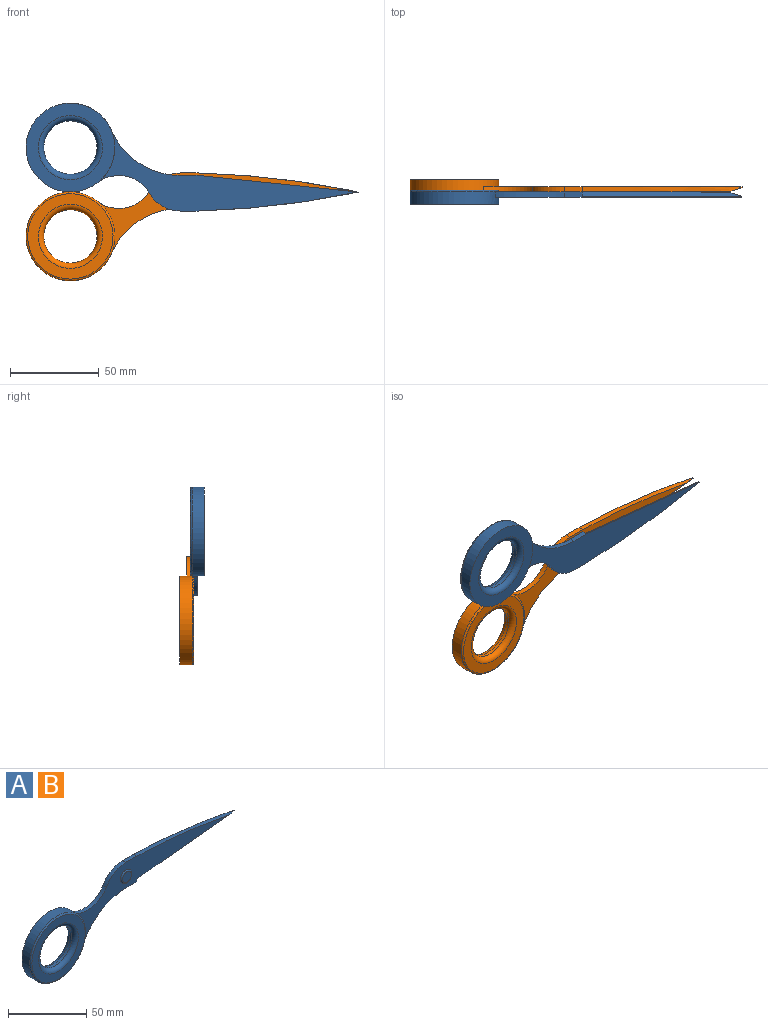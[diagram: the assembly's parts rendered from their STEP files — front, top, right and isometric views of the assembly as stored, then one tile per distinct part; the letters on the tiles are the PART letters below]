
ASSEMBLY  parts=2 mates=1
PART A: 20 faces, bbox 188.9x8x62.8 mm
  f0: plane 138.19x45.59mm, normal (0,-1,0), area 1559.5mm2, adj f1,f3,f4,f6,f7,f9,f14,f15
  f1: cylinder r=20mm len=27.95mm, axis (0,1,0), area 95.5mm2, adj f0,f2,f4,f5
  f2: plane 145.66x45.59mm, normal (0,1,0), area 1836.2mm2, adj f1,f3,f4,f5,f6,f7,f8,f9
  f3: plane 10x3mm, normal (0,0,1), area 30mm2, adj f0,f2,f4,f9
  f4: cylinder r=20mm len=17.71mm, axis (0,1,0), area 65.2mm2, adj f0,f1,f2,f3
  f5: cylinder r=25mm len=50mm, axis (0,1,0), area 1004mm2, adj f1,f2,f6,f11,f17
  f6: cylinder r=42.31mm len=38.86mm, axis (0,1,0), area 147.8mm2, adj f0,f2,f5,f7
  f7: plane 10x3mm, normal (0,0,-1), area 30mm2, adj f0,f2,f6,f8,f14
  f8: plane 90x9.3mm, normal (0.1,0,-0.99), area 63.7mm2, adj f2,f7,f9,f15
  f9: cylinder r=500mm len=90mm, axis (0,1,0), area 263.6mm2, adj f0,f2,f3,f8,f15
  f10: plane 48x48mm, normal (0,-1,0), area 791.7mm2, adj f16,f17
  f11: plane 50x50mm, normal (0,1,0), area 945.6mm2, adj f5,f18
  f12: cylinder r=15mm len=30mm, axis (0,1,0), area 188.5mm2, adj f16,f18
  f13: plane 8x8mm, normal (0,-1,0), area 50.3mm2, adj f19
  f14: plane 2.3x2.3mm, normal (1,0,0), area 2.6mm2, adj f0,f7,f15
  f15: plane 90x10.82mm, normal (0.07,-0.71,-0.71), area 281mm2, adj f0,f8,f9,f14
  f16: torus R=18mm, axis (0,-1,0), area 476.4mm2, adj f10,f12
  f17: torus R=24mm, axis (0,-1,0), area 243.2mm2, adj f0,f5,f10
  f18: torus R=18mm, axis (0,-1,0), area 476.4mm2, adj f11,f12
  f19: torus R=4mm, axis (0,-1,0), area 45.8mm2, adj f0,f13
PART B: same geometry as A
PLACE A rot(axis=(1,0,0),180deg) t=(-15.79,5.73,46.13)mm
PLACE B t=(-15.79,11.73,46.13)mm fixed
MATE revolute B.f0 <-> A.f0  axis (0,-1,0) through (-33.5,8.73,46.13)mm
